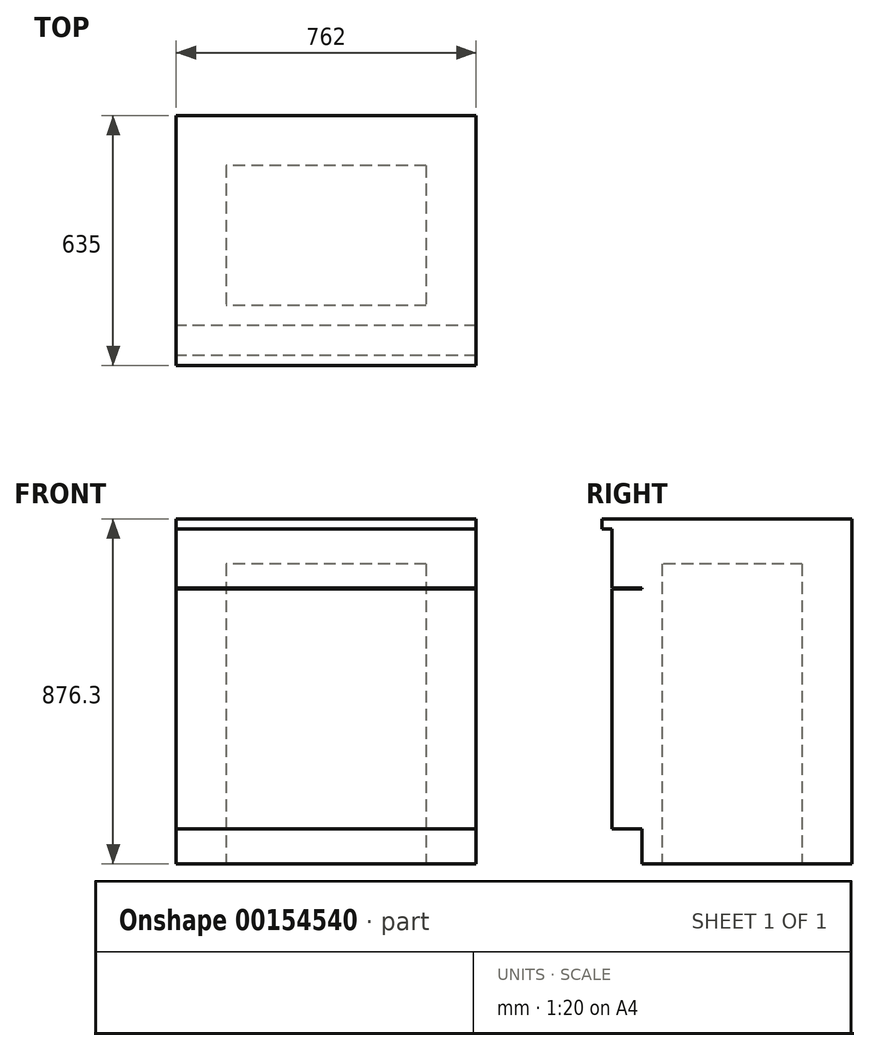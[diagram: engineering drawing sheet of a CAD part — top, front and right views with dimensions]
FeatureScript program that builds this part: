
annotation { "Feature Type Name" : "Feature", "Feature Type Description" : "" }
export const myFeature = defineFeature(function(context is Context, id is Id, definition is map)
    precondition{}
    {
        {
            var Q0;
            Q0=qCreatedBy(makeId("Top.planeOp"),FACE);
            var sketch = newSketch(context, id + "F0", { "sketchPlane" : qUnion([Q0])});
            skLineSegment(sketch, "E0.bottom", {"start": v(381, 304.8) * mm, "end": v(-381, 304.8) * mm});
            skLineSegment(sketch, "E0.top", {"start": v(381, -304.8) * mm, "end": v(-381, -304.8) * mm});
            skLineSegment(sketch, "E0.left", {"start": v(381, 304.8) * mm, "end": v(381, -304.8) * mm});
            skLineSegment(sketch, "E0.right", {"start": v(-381, 304.8) * mm, "end": v(-381, -304.8) * mm});
            skPoint(sketch, "E0.middle", {"position": v(0, 0) * mm});
            skSolve(sketch);
        }
        {
            var Q0;
            Q0=makeQuery(id+"F0.imprint","IMPRINT",FACE,{"disambiguationData":[TD([[makeQuery(id+"F0.imprint","IMPRINT",EDGE,{"derivedFrom":sQuery(id+"F0.wireOp",EDGE,"E0.bottom")}),1.0]])]});
            extrude(context, id + "F1", {"entities" : qUnion([Q0]), "depth" : 876.3 * mm});
        }
        {
            var Q0;
            Q0=makeQuery(id+"F1.opExtrude","SWEPT_FACE",FACE,{"disambiguationData":[OSD([sQuery(id+"F0.wireOp",EDGE,"E0.top")])]});
            var sketch = newSketch(context, id + "F2", { "sketchPlane" : qUnion([Q0])});
            skLineSegment(sketch, "E1.bottom", {"start": v(-381, 0) * mm, "end": v(381, 0) * mm});
            skLineSegment(sketch, "E1.top", {"start": v(-381, 88.9) * mm, "end": v(381, 88.9) * mm});
            skLineSegment(sketch, "E1.left", {"start": v(-381, 0) * mm, "end": v(-381, 88.9) * mm});
            skLineSegment(sketch, "E1.right", {"start": v(381, 0) * mm, "end": v(381, 88.9) * mm});
            skLineSegment(sketch, "E2.bottom", {"start": v(-1.27, 88.9) * mm, "end": v(1.27, 88.9) * mm});
            skLineSegment(sketch, "E2.top", {"start": v(-1.27, 698.5) * mm, "end": v(1.27, 698.5) * mm});
            skLineSegment(sketch, "E2.left", {"start": v(-1.27, 88.9) * mm, "end": v(-1.27, 698.5) * mm});
            skLineSegment(sketch, "E2.right", {"start": v(1.27, 88.9) * mm, "end": v(1.27, 698.5) * mm});
            skLineSegment(sketch, "E3.bottom", {"start": v(-381, 698.5) * mm, "end": v(381, 698.5) * mm});
            skLineSegment(sketch, "E3.top", {"start": v(-381, 701.04) * mm, "end": v(381, 701.04) * mm});
            skLineSegment(sketch, "E3.left", {"start": v(-381, 698.5) * mm, "end": v(-381, 701.04) * mm});
            skLineSegment(sketch, "E3.right", {"start": v(381, 698.5) * mm, "end": v(381, 701.04) * mm});
            skLineSegment(sketch, "E4", {"start": v(0, 698.5) * mm, "end": v(0, 876.3) * mm, "construction": true});
            skSolve(sketch);
        }
        {
            var Q0;
            Q0=makeQuery(id+"F2.imprint","IMPRINT",FACE,{"disambiguationData":[TD([[makeQuery(id+"F2.imprint","IMPRINT",EDGE,{"derivedFrom":sQuery(id+"F2.wireOp",EDGE,"E1.bottom")}),-1.0]])]});
            var Q1;
            Q1=makeQuery(id+"F2.imprint","IMPRINT",FACE,{"disambiguationData":[TD([[makeQuery(id+"F2.imprint","IMPRINT",EDGE,{"derivedFrom":sQuery(id+"F2.wireOp",EDGE,"E3.top")}),-1.0]])]});
            var Q2;
            Q2=makeQuery(id+"F2.imprint","IMPRINT",FACE,{"disambiguationData":[TD([[makeQuery(id+"F2.imprint","IMPRINT",EDGE,{"derivedFrom":sQuery(id+"F2.wireOp",EDGE,"E2.bottom")}),1.0]])]});
            extrude(context, id + "F3", {"entities" : qUnion([Q0, Q1, Q2]), "operationType" : NewBodyOperationType.REMOVE, "oppositeDirection" : true, "depth" : 76.2 * mm});
        }
        {
            var Q0;
            Q0=makeQuery(id+"F1.opExtrude","CAP_FACE",FACE,{"disambiguationData":[OSD([sQuery(id+"F0.wireOp",EDGE,"E0.bottom"),sQuery(id+"F0.wireOp",EDGE,"E0.top"),sQuery(id+"F0.wireOp",EDGE,"E0.left"),sQuery(id+"F0.wireOp",EDGE,"E0.right")])],"isStart":false});
            var sketch = newSketch(context, id + "F4", { "sketchPlane" : qUnion([Q0])});
            skLineSegment(sketch, "E5.bottom", {"start": v(-381, 304.8) * mm, "end": v(381, 304.8) * mm});
            skLineSegment(sketch, "E5.top", {"start": v(-381, -330.2) * mm, "end": v(381, -330.2) * mm});
            skLineSegment(sketch, "E5.left", {"start": v(-381, 304.8) * mm, "end": v(-381, -330.2) * mm});
            skLineSegment(sketch, "E5.right", {"start": v(381, 304.8) * mm, "end": v(381, -330.2) * mm});
            skSolve(sketch);
        }
        {
            var Q0;
            {var subQ0=sQuery(id+"F4.wireOp",EDGE,"E5.top");Q0=makeQuery(id+"F4.imprint","IMPRINT",FACE,{"disambiguationData":[TD([[makeQuery(id+"F4.imprint","IMPRINT",EDGE,{"derivedFrom":subQ0}),1.0]])]});}
            var Q1;
            {var subQ0=sQuery(id+"F4.wireOp",EDGE,"E5.bottom");Q1=makeQuery(id+"F4.imprint","IMPRINT",FACE,{"disambiguationData":[TD([[makeQuery(id+"F4.imprint","IMPRINT",EDGE,{"derivedFrom":subQ0}),1.0]])]});}
            extrude(context, id + "F5", {"entities" : qUnion([Q0, Q1]), "operationType" : NewBodyOperationType.ADD, "oppositeDirection" : true, "depth" : 25.4 * mm});
        }
        {
            var Q0;
            Q0=makeQuery(id+"F1.opExtrude","CAP_FACE",FACE,{"disambiguationData":[OSD([sQuery(id+"F0.wireOp",EDGE,"E0.bottom"),sQuery(id+"F0.wireOp",EDGE,"E0.top"),sQuery(id+"F0.wireOp",EDGE,"E0.left"),sQuery(id+"F0.wireOp",EDGE,"E0.right")])],"isStart":true});
            var sketch = newSketch(context, id + "F6", { "sketchPlane" : qUnion([Q0])});
            skLineSegment(sketch, "E6.bottom", {"start": v(254, -177.8) * mm, "end": v(-254, -177.8) * mm});
            skLineSegment(sketch, "E6.top", {"start": v(254, 177.8) * mm, "end": v(-254, 177.8) * mm});
            skLineSegment(sketch, "E6.left", {"start": v(254, -177.8) * mm, "end": v(254, 177.8) * mm});
            skLineSegment(sketch, "E6.right", {"start": v(-254, -177.8) * mm, "end": v(-254, 177.8) * mm});
            skSolve(sketch);
        }
        {
            var Q0;
            Q0=makeQuery(id+"F6.imprint","IMPRINT",FACE,{"disambiguationData":[TD([[makeQuery(id+"F6.imprint","IMPRINT",EDGE,{"derivedFrom":sQuery(id+"F6.wireOp",EDGE,"E6.bottom")}),-1.0]])]});
            extrude(context, id + "F7", {"entities" : qUnion([Q0]), "operationType" : NewBodyOperationType.REMOVE, "oppositeDirection" : true, "depth" : 762 * mm});
        }
    });
